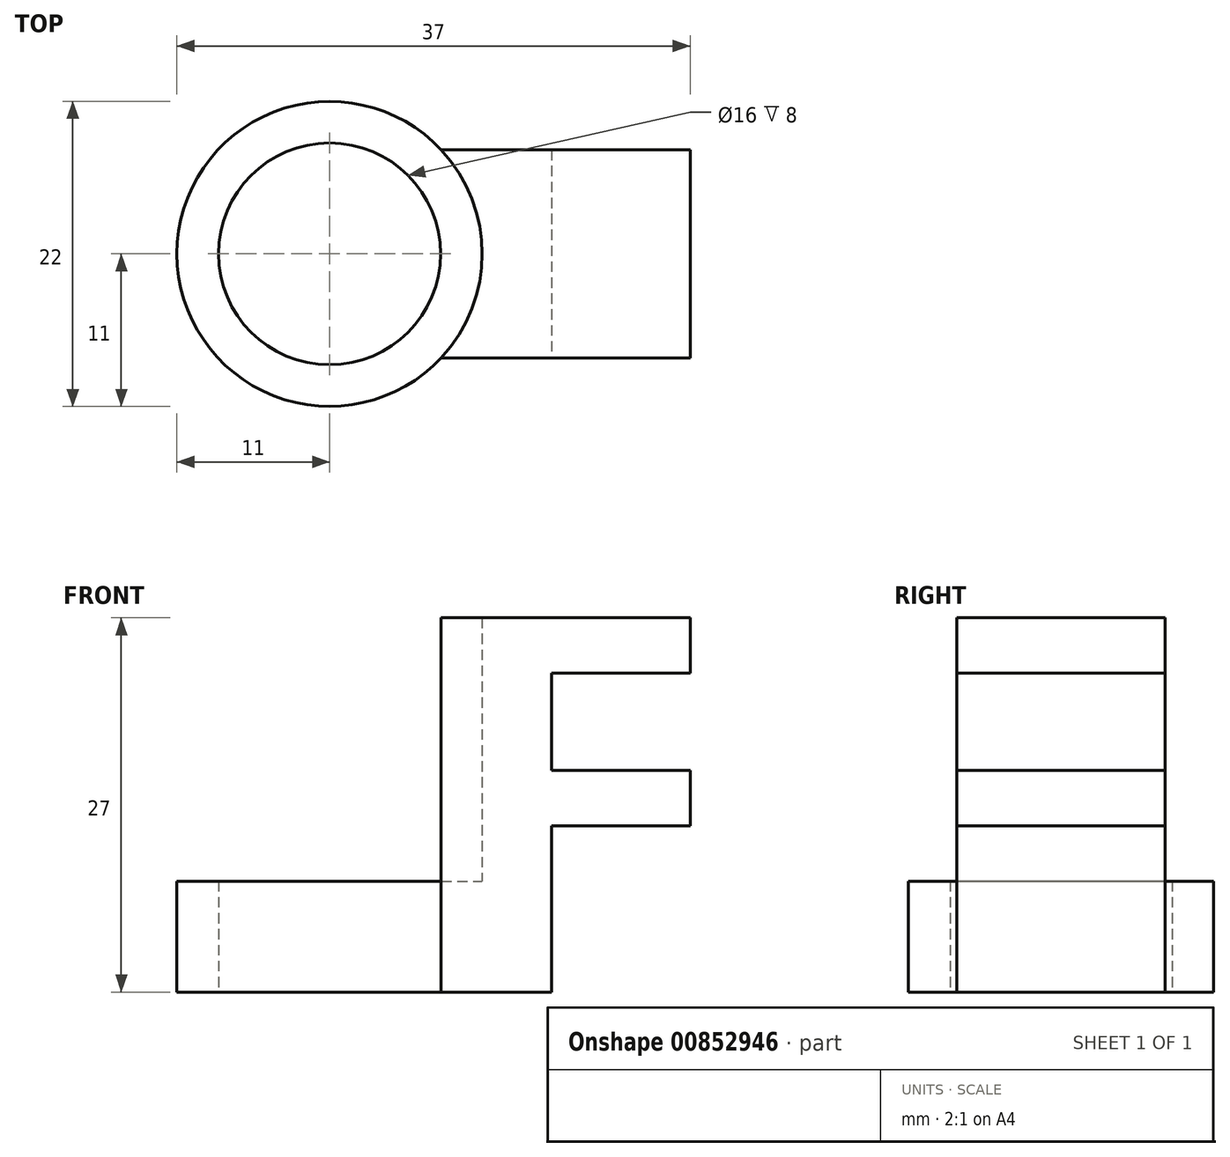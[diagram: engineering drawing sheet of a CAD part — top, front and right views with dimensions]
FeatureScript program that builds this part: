
annotation { "Feature Type Name" : "Feature", "Feature Type Description" : "" }
export const myFeature = defineFeature(function(context is Context, id is Id, definition is map)
    precondition{}
    {
        {
            var Q0;
            Q0=qCreatedBy(makeId("Top.planeOp"),FACE);
            var sketch = newSketch(context, id + "F0", { "sketchPlane" : qUnion([Q0])});
            skCircle(sketch, "E0", {"center": v(0, 0) * mm, "radius": 8 * mm});
            skCircle(sketch, "E1", {"center": v(0, 0) * mm, "radius": 11 * mm});
            skLineSegment(sketch, "E2", {"start": v(0, 0) * mm, "end": v(16, 0) * mm});
            skLineSegment(sketch, "E3.bottom", {"start": v(16, 0) * mm, "end": v(10, 0) * mm});
            skLineSegment(sketch, "E3.top", {"start": v(16, -7.5) * mm, "end": v(6, -7.5) * mm});
            skPoint(sketch, "E4.oppositeSnap0", {"position": v(6, -3.75) * mm});
            skLineSegment(sketch, "E4.top", {"start": v(16, 7.5) * mm, "end": v(6, 7.5) * mm});
            skLineSegment(sketch, "E5", {"start": v(16, 0) * mm, "end": v(16, -7.5) * mm});
            skLineSegment(sketch, "E6", {"start": v(16, 0) * mm, "end": v(16, 7.5) * mm});
            skSolve(sketch);
        }
        {
            var Q0;
            Q0 = qSketchRegion(id + "F0", true);
            extrude(context, id + "F1", {"entities" : qUnion([Q0]), "depth" : 8 * mm, "offsetDistance" : 25 * mm});
        }
        {
            var Q0;
            Q0=makeQuery(id+"F0.imprint","IMPRINT",FACE,{"disambiguationData":[TD([[makeQuery(id+"F0.imprint","IMPRINT",EDGE,{"derivedFrom":sQuery(id+"F0.wireOp",EDGE,"E4.top")}),1.0]])]});
            var Q1;
            Q1=makeQuery(id+"F0.imprint","IMPRINT",FACE,{"disambiguationData":[TD([[makeQuery(id+"F0.imprint","IMPRINT",EDGE,{"derivedFrom":sQuery(id+"F0.wireOp",EDGE,"E3.top")}),-1.0]])]});
            extrude(context, id + "F2", {"entities" : qUnion([Q0, Q1]), "operationType" : NewBodyOperationType.ADD, "depth" : 27 * mm, "offsetDistance" : 25 * mm});
        }
        {
            var Q0;
            {var subQ0=sQuery(id+"F0.wireOp",EDGE,"E6");var subQ1=sQuery(id+"F0.wireOp",EDGE,"E5");Q0=makeQuery(id+"F2.boolean.opBoolean","MERGE",FACE,{"derivedFrom":[makeQuery(id+"F1.opExtrude","SWEPT_FACE",FACE,{"disambiguationData":[OSD([subQ1,subQ0])]}),makeQuery(id+"F2.opExtrude","SWEPT_FACE",FACE,{"disambiguationData":[OSD([subQ1,subQ0])]})]});}
            var sketch = newSketch(context, id + "F3", { "sketchPlane" : qUnion([Q0])});
            skLineSegment(sketch, "E7.bottom", {"start": v(7.5, 27) * mm, "end": v(-7.5, 27) * mm});
            skLineSegment(sketch, "E7.top", {"start": v(7.5, 23) * mm, "end": v(-7.5, 23) * mm});
            skLineSegment(sketch, "E7.left", {"start": v(7.5, 27) * mm, "end": v(7.5, 23) * mm});
            skLineSegment(sketch, "E7.right", {"start": v(-7.5, 27) * mm, "end": v(-7.5, 23) * mm});
            skSolve(sketch);
        }
        {
            var Q0;
            Q0=makeQuery(id+"F3.imprint","IMPRINT",FACE,{"disambiguationData":[TD([[makeQuery(id+"F3.imprint","IMPRINT",EDGE,{"derivedFrom":sQuery(id+"F3.wireOp",EDGE,"E7.bottom")}),-1.0]])]});
            extrude(context, id + "F4", {"entities" : qUnion([Q0]), "operationType" : NewBodyOperationType.ADD, "depth" : 10 * mm, "offsetDistance" : 25 * mm});
        }
        {
            var Q0;
            {var subQ0=sQuery(id+"F0.wireOp",EDGE,"E6");var subQ1=sQuery(id+"F0.wireOp",EDGE,"E5");Q0=makeQuery(id+"F2.boolean.opBoolean","MERGE",FACE,{"derivedFrom":[makeQuery(id+"F1.opExtrude","SWEPT_FACE",FACE,{"disambiguationData":[OSD([subQ1,subQ0])]}),makeQuery(id+"F2.opExtrude","SWEPT_FACE",FACE,{"disambiguationData":[OSD([subQ1,subQ0])]})]});}
            var sketch = newSketch(context, id + "F5", { "sketchPlane" : qUnion([Q0])});
            skLineSegment(sketch, "E8.bottom", {"start": v(7.5, 23) * mm, "end": v(-7.5, 23) * mm});
            skLineSegment(sketch, "E8.top", {"start": v(7.5, 16) * mm, "end": v(-7.5, 16) * mm});
            skLineSegment(sketch, "E8.left", {"start": v(7.5, 23) * mm, "end": v(7.5, 16) * mm});
            skLineSegment(sketch, "E8.right", {"start": v(-7.5, 23) * mm, "end": v(-7.5, 16) * mm});
            skLineSegment(sketch, "E9.top", {"start": v(7.5, 12) * mm, "end": v(-7.5, 12) * mm});
            skLineSegment(sketch, "E9.left", {"start": v(7.5, 16) * mm, "end": v(7.5, 12) * mm});
            skLineSegment(sketch, "E9.right", {"start": v(-7.5, 16) * mm, "end": v(-7.5, 12) * mm});
            skSolve(sketch);
        }
        {
            var Q0;
            Q0=makeQuery(id+"F5.imprint","IMPRINT",FACE,{"disambiguationData":[TD([[makeQuery(id+"F5.imprint","IMPRINT",EDGE,{"derivedFrom":sQuery(id+"F5.wireOp",EDGE,"E8.top")}),1.0]])]});
            extrude(context, id + "F6", {"entities" : qUnion([Q0]), "operationType" : NewBodyOperationType.ADD, "depth" : 10 * mm, "offsetDistance" : 25 * mm});
        }
    });
